# Revit family: Legrand_Gestion_eclairage_Detecteur_mouvement_Plafond_autonome
name_source: partatom
category: Dispositifs d'éclairage
units: mm (PartAtom-declared; Revit-internal decimal feet)

## family parameters
Conserver l'orientation des annotations = Non
Cote de connecteur circulaire = Utiliser le diamètre
Couper avec des vides une fois chargée = Non
Hôte = Face
Partagée = Non
Point de calcul de pièce = Non
Type d'élément = Normal

## types (2) — shared parameters
Adapté pour transmission sans fil = Non
Angle de détection horizontal (MAX) (°) = 360
Collecteur de terre = Non
Condition Générale d'Utilisation = https://export.legrand.com
Cosses d'artère secondaire = Non
Couleur = Blanc
Coupure forcée = Non
Diamètre de détection sur le plancher (m) = 8
Elévation par défaut = 1219 mm
Entrée secondaire = Non
Fabricant = Legrand
Fonction variateur intégré = Non
Fréquence (MAX) (Hz) = 60
Fréquence (MIN) (Hz) = 50
Gestion CVC = Non
Gestion alarme = Non
Hauteur de montage maximale (m) = 2.5
Liaison neutre = Non
Réglage de lumière constante = Oui
Sensibilité lumineuse (MAX) (lx) = 1275
Sensibilité lumineuse réglable = Oui
Température (MIN) (°C) = -5
Type de tension = CA
Télécommandable = Non
URL = http://www.legrandoc.com

## per-type parameters (varying)
| type | Angle de détection horizontal (MIN) (°) | Capacité de coupure max. (W) | Classe de protection (IP) | Courant de démarrage max. (A) | Description | Durée d'enclenchement max. (mn) | Durée d'enclenchement min. (s) | Exécution - Modèle | Mode de montage | Modèle | Numéro RAL | Portée max. frontale (m) | Portée max. latérale (m) | Sensibilité lumineuse (MIN) (lx) | Sensibilité réglable | Température (MAX) (°C) | Tension nominale (V) |
| PIR - Applique - 360° - 45m² | 360 | 0 | IP20 | 0 | DETECTEUR PIR 360° MONTAGE AU PLAFOND EN SAILLIE | 10 | 10 | détecteur de présence | apparent | 048948 | 9006 | 8 | 8 | 10 | Oui | 35 | 240 |
| PIR - Encastré - 360° - 45m² | 0 | 2000 | IP41 | 8.5 | Détect autonome ECO 1 Prog Mosaic-1 circuit éclairage-faux plafond-45m² | 30 | 5 | détecteur de mouvement | encastré | 048899 | 9003 | 6 | 4 | 5 | Non | 45 | 230 |
